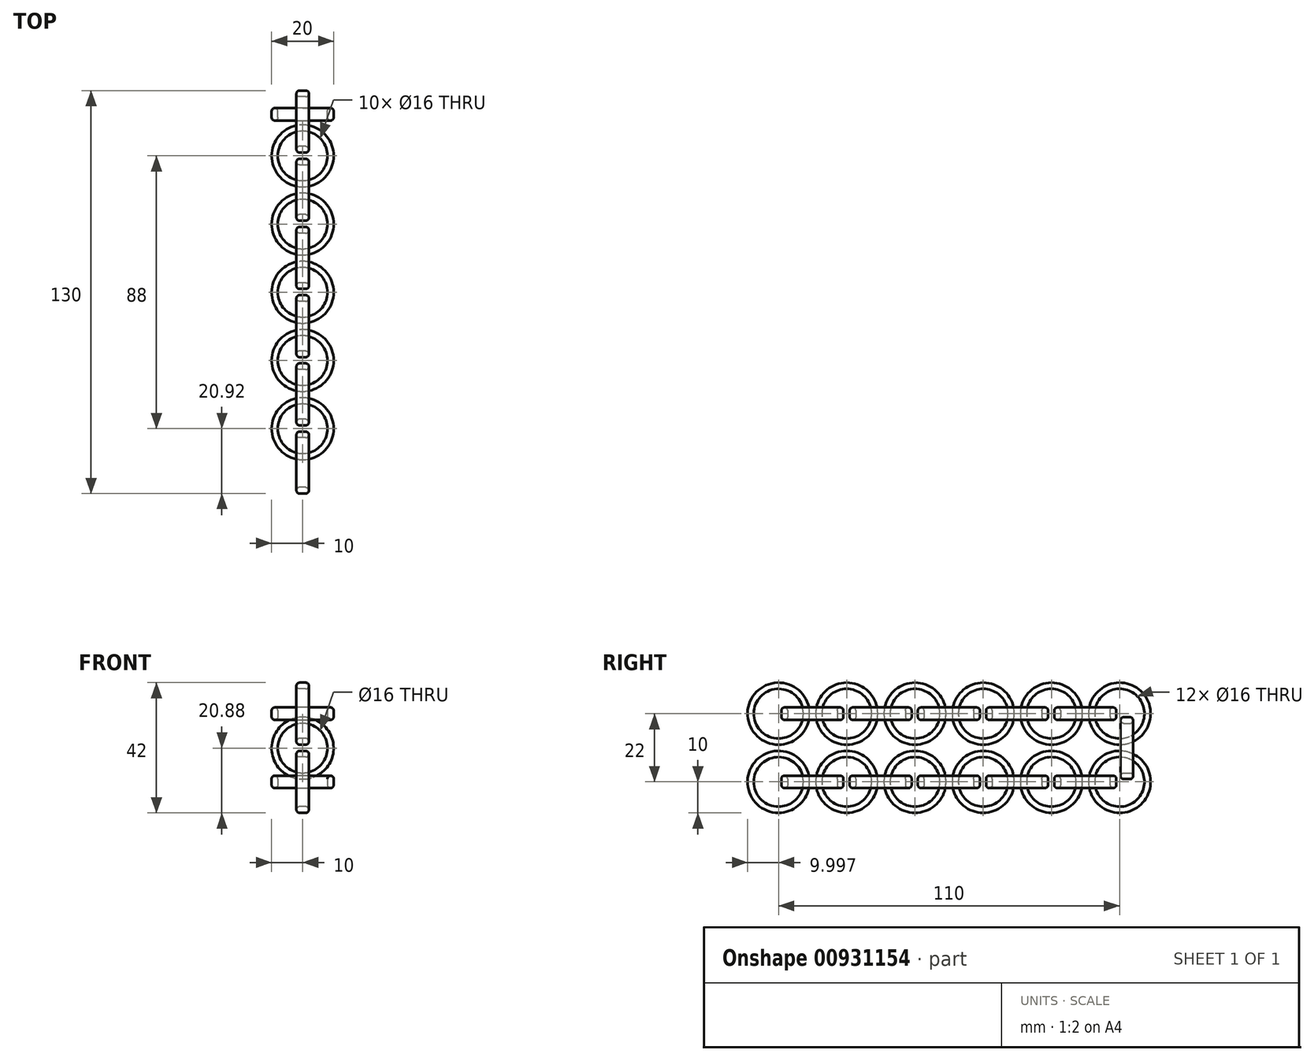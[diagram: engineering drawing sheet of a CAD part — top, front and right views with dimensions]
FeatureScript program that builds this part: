
annotation { "Feature Type Name" : "Feature", "Feature Type Description" : "" }
export const myFeature = defineFeature(function(context is Context, id is Id, definition is map)
    precondition{}
    {
        {
            var Q0;
            Q0=qCreatedBy(makeId("Top.planeOp"),FACE);
            var sketch = newSketch(context, id + "F0", { "sketchPlane" : qUnion([Q0])});
            skCircle(sketch, "E0", {"center": v(0, 0) * mm, "radius": 10 * mm});
            skCircle(sketch, "E1", {"center": v(0, 0) * mm, "radius": 8 * mm});
            skSolve(sketch);
        }
        {
            var Q0;
            Q0=makeQuery(id+"F0.imprint","IMPRINT",FACE,{"disambiguationData":[TD([[makeQuery(id+"F0.imprint","IMPRINT",EDGE,{"derivedFrom":sQuery(id+"F0.wireOp",EDGE,"E0")}),1.0]])]});
            extrude(context, id + "F1", {"entities" : qUnion([Q0]), "endBound" : BoundingType.SYMMETRIC, "depth" : 4 * mm, "offsetDistance" : 25 * mm});
        }
        {
            var Q0;
            Q0=makeQuery(id+"F1.opExtrude","CAP_EDGE",EDGE,{"disambiguationData":[OSD([sQuery(id+"F0.wireOp",EDGE,"E0")])],"isStart":false});
            var Q1;
            Q1=makeQuery(id+"F1.opExtrude","CAP_EDGE",EDGE,{"disambiguationData":[OSD([sQuery(id+"F0.wireOp",EDGE,"E1")])],"isStart":false});
            fillet(context, id + "F2", {"entities" : qUnion([Q0, Q1]), "radius" : 1 * mm, "tangentPropagation" : true, "allowEdgeOverflow" : false});
        }
        {
            var Q0;
            Q0=makeQuery(id+"F1.opExtrude","CAP_EDGE",EDGE,{"disambiguationData":[OSD([sQuery(id+"F0.wireOp",EDGE,"E0")])],"isStart":true});
            var Q1;
            Q1=makeQuery(id+"F1.opExtrude","CAP_EDGE",EDGE,{"disambiguationData":[OSD([sQuery(id+"F0.wireOp",EDGE,"E1")])],"isStart":true});
            fillet(context, id + "F3", {"entities" : qUnion([Q0, Q1]), "radius" : 1 * mm, "tangentPropagation" : true, "allowEdgeOverflow" : false});
        }
        {
            var Q0;
            Q0=makeQuery(id+"F1.opExtrude","SWEPT_BODY",BODY,{"disambiguationData":[OSD([sQuery(id+"F0.wireOp",EDGE,"E0"),sQuery(id+"F0.wireOp",EDGE,"E1")])]});
            transform(context, id + "F4", {"entities" : qUnion([Q0]), "transformType" : TransformType.TRANSLATION_3D, "dx" : 0 * mm, "dy" : 22 * mm, "dz" : 0 * mm, "makeCopy" : true});
        }
        {
            var Q0;
            Q0=makeQuery(id+"F1.opExtrude","SWEPT_BODY",BODY,{"disambiguationData":[OSD([sQuery(id+"F0.wireOp",EDGE,"E0"),sQuery(id+"F0.wireOp",EDGE,"E1")])]});
            transform(context, id + "F5", {"entities" : qUnion([Q0]), "transformType" : TransformType.TRANSLATION_3D, "dx" : 0 * mm, "dy" : 44 * mm, "dz" : 0 * mm, "makeCopy" : true});
        }
        {
            var Q0;
            Q0=makeQuery(id+"F1.opExtrude","SWEPT_BODY",BODY,{"disambiguationData":[OSD([sQuery(id+"F0.wireOp",EDGE,"E0"),sQuery(id+"F0.wireOp",EDGE,"E1")])]});
            transform(context, id + "F6", {"entities" : qUnion([Q0]), "transformType" : TransformType.TRANSLATION_3D, "dx" : 0 * mm, "dy" : -22 * mm, "dz" : 0 * mm, "makeCopy" : true});
        }
        {
            var Q0;
            Q0=makeQuery(id+"F1.opExtrude","SWEPT_BODY",BODY,{"disambiguationData":[OSD([sQuery(id+"F0.wireOp",EDGE,"E0"),sQuery(id+"F0.wireOp",EDGE,"E1")])]});
            transform(context, id + "F7", {"entities" : qUnion([Q0]), "transformType" : TransformType.TRANSLATION_3D, "dx" : 0 * mm, "dy" : -44 * mm, "dz" : 0 * mm, "makeCopy" : true});
        }
        {
            var Q0;
            Q0=makeQuery(id+"F1.opExtrude","SWEPT_BODY",BODY,{"disambiguationData":[OSD([sQuery(id+"F0.wireOp",EDGE,"E0"),sQuery(id+"F0.wireOp",EDGE,"E1")])]});
            transform(context, id + "F8", {"entities" : qUnion([Q0]), "transformType" : TransformType.TRANSLATION_3D, "dx" : 0 * mm, "dy" : -10.6 * mm, "dz" : 0.3 * mm, "makeCopy" : true});
        }
        {
            var Q0;
            Q0=makeQuery(id+"F8.opPattern","COPY",BODY,{"derivedFrom":makeQuery(id+"F1.opExtrude","SWEPT_BODY",BODY,{"disambiguationData":[OSD([sQuery(id+"F0.wireOp",EDGE,"E0"),sQuery(id+"F0.wireOp",EDGE,"E1")])]}),"instanceName":"1"});
            deleteBodies(context, id + "F9", {"entities" : qUnion([Q0])});
        }
        {
            var Q0;
            Q0=qCreatedBy(makeId("Right.planeOp"),FACE);
            var sketch = newSketch(context, id + "F10", { "sketchPlane" : qUnion([Q0])});
            skCircle(sketch, "E2", {"center": v(-10.92, 0) * mm, "radius": 10 * mm});
            skCircle(sketch, "E3", {"center": v(-10.92, 0) * mm, "radius": 8 * mm});
            skSolve(sketch);
        }
        {
            var Q0;
            Q0=makeQuery(id+"F10.imprint","IMPRINT",FACE,{"disambiguationData":[TD([[makeQuery(id+"F10.imprint","IMPRINT",EDGE,{"derivedFrom":sQuery(id+"F10.wireOp",EDGE,"E2")}),1.0]])]});
            extrude(context, id + "F11", {"entities" : qUnion([Q0]), "endBound" : BoundingType.SYMMETRIC, "depth" : 4 * mm, "offsetDistance" : 25 * mm});
        }
        {
            var Q0;
            Q0=makeQuery(id+"F11.opExtrude","CAP_EDGE",EDGE,{"disambiguationData":[OSD([sQuery(id+"F10.wireOp",EDGE,"E2")])],"isStart":false});
            var Q1;
            Q1=makeQuery(id+"F11.opExtrude","CAP_EDGE",EDGE,{"disambiguationData":[OSD([sQuery(id+"F10.wireOp",EDGE,"E3")])],"isStart":false});
            var Q2;
            Q2=makeQuery(id+"F11.opExtrude","CAP_EDGE",EDGE,{"disambiguationData":[OSD([sQuery(id+"F10.wireOp",EDGE,"E3")])],"isStart":true});
            var Q3;
            Q3=makeQuery(id+"F11.opExtrude","CAP_EDGE",EDGE,{"disambiguationData":[OSD([sQuery(id+"F10.wireOp",EDGE,"E2")])],"isStart":true});
            fillet(context, id + "F12", {"entities" : qUnion([Q0, Q1, Q2, Q3]), "radius" : 1 * mm, "tangentPropagation" : true, "allowEdgeOverflow" : false});
        }
        {
            var Q0;
            Q0=makeQuery(id+"F11.opExtrude","SWEPT_BODY",BODY,{"disambiguationData":[OSD([sQuery(id+"F10.wireOp",EDGE,"E2"),sQuery(id+"F10.wireOp",EDGE,"E3")])]});
            transform(context, id + "F13", {"entities" : qUnion([Q0]), "transformType" : TransformType.TRANSLATION_3D, "dx" : 0 * mm, "dy" : 22 * mm, "dz" : 0 * mm, "makeCopy" : true});
        }
        {
            var Q0;
            Q0=makeQuery(id+"F11.opExtrude","SWEPT_BODY",BODY,{"disambiguationData":[OSD([sQuery(id+"F10.wireOp",EDGE,"E2"),sQuery(id+"F10.wireOp",EDGE,"E3")])]});
            transform(context, id + "F14", {"entities" : qUnion([Q0]), "transformType" : TransformType.TRANSLATION_3D, "dx" : 0 * mm, "dy" : 44 * mm, "dz" : 0 * mm, "makeCopy" : true});
        }
        {
            var Q0;
            Q0=makeQuery(id+"F11.opExtrude","SWEPT_BODY",BODY,{"disambiguationData":[OSD([sQuery(id+"F10.wireOp",EDGE,"E2"),sQuery(id+"F10.wireOp",EDGE,"E3")])]});
            transform(context, id + "F15", {"entities" : qUnion([Q0]), "transformType" : TransformType.TRANSLATION_3D, "dx" : 0 * mm, "dy" : -22 * mm, "dz" : 0 * mm, "makeCopy" : true});
        }
        {
            var Q0;
            Q0=makeQuery(id+"F11.opExtrude","SWEPT_BODY",BODY,{"disambiguationData":[OSD([sQuery(id+"F10.wireOp",EDGE,"E2"),sQuery(id+"F10.wireOp",EDGE,"E3")])]});
            transform(context, id + "F16", {"entities" : qUnion([Q0]), "transformType" : TransformType.TRANSLATION_3D, "dx" : 0 * mm, "dy" : -44 * mm, "dz" : 0 * mm, "makeCopy" : true});
        }
        {
            var Q0;
            Q0=makeQuery(id+"F11.opExtrude","SWEPT_BODY",BODY,{"disambiguationData":[OSD([sQuery(id+"F10.wireOp",EDGE,"E2"),sQuery(id+"F10.wireOp",EDGE,"E3")])]});
            transform(context, id + "F17", {"entities" : qUnion([Q0]), "transformType" : TransformType.TRANSLATION_3D, "dx" : 0 * mm, "dy" : 66 * mm, "dz" : 0 * mm, "makeCopy" : true});
        }
        {
            var Q0;
            Q0=makeQuery(id+"F16.opPattern","COPY",BODY,{"derivedFrom":makeQuery(id+"F11.opExtrude","SWEPT_BODY",BODY,{"disambiguationData":[OSD([sQuery(id+"F10.wireOp",EDGE,"E2"),sQuery(id+"F10.wireOp",EDGE,"E3")])]}),"instanceName":"1"});
            transform(context, id + "F18", {"entities" : qUnion([Q0]), "transformType" : TransformType.TRANSLATION_3D, "dx" : 0 * mm, "dy" : 0 * mm, "dz" : 22 * mm, "makeCopy" : true});
        }
        {
            var Q0;
            Q0=makeQuery(id+"F18.opPattern","COPY",BODY,{"derivedFrom":makeQuery(id+"F16.opPattern","COPY",BODY,{"derivedFrom":makeQuery(id+"F11.opExtrude","SWEPT_BODY",BODY,{"disambiguationData":[OSD([sQuery(id+"F10.wireOp",EDGE,"E2"),sQuery(id+"F10.wireOp",EDGE,"E3")])]}),"instanceName":"1"}),"instanceName":"1"});
            transform(context, id + "F19", {"entities" : qUnion([Q0]), "transformType" : TransformType.TRANSLATION_3D, "dx" : 0 * mm, "dy" : 22 * mm, "dz" : 0 * mm, "makeCopy" : true});
        }
        {
            var Q0;
            Q0=makeQuery(id+"F19.opPattern","COPY",BODY,{"derivedFrom":makeQuery(id+"F18.opPattern","COPY",BODY,{"derivedFrom":makeQuery(id+"F16.opPattern","COPY",BODY,{"derivedFrom":makeQuery(id+"F11.opExtrude","SWEPT_BODY",BODY,{"disambiguationData":[OSD([sQuery(id+"F10.wireOp",EDGE,"E2"),sQuery(id+"F10.wireOp",EDGE,"E3")])]}),"instanceName":"1"}),"instanceName":"1"}),"instanceName":"1"});
            transform(context, id + "F20", {"entities" : qUnion([Q0]), "transformType" : TransformType.TRANSLATION_3D, "dx" : 0 * mm, "dy" : 22 * mm, "dz" : 0 * mm, "makeCopy" : true});
        }
        {
            var Q0;
            Q0=makeQuery(id+"F19.opPattern","COPY",BODY,{"derivedFrom":makeQuery(id+"F18.opPattern","COPY",BODY,{"derivedFrom":makeQuery(id+"F16.opPattern","COPY",BODY,{"derivedFrom":makeQuery(id+"F11.opExtrude","SWEPT_BODY",BODY,{"disambiguationData":[OSD([sQuery(id+"F10.wireOp",EDGE,"E2"),sQuery(id+"F10.wireOp",EDGE,"E3")])]}),"instanceName":"1"}),"instanceName":"1"}),"instanceName":"1"});
            transform(context, id + "F21", {"entities" : qUnion([Q0]), "transformType" : TransformType.TRANSLATION_3D, "dx" : 0 * mm, "dy" : 44 * mm, "dz" : 0 * mm, "makeCopy" : true});
        }
        {
            var Q0;
            Q0=makeQuery(id+"F20.opPattern","COPY",BODY,{"derivedFrom":makeQuery(id+"F19.opPattern","COPY",BODY,{"derivedFrom":makeQuery(id+"F18.opPattern","COPY",BODY,{"derivedFrom":makeQuery(id+"F16.opPattern","COPY",BODY,{"derivedFrom":makeQuery(id+"F11.opExtrude","SWEPT_BODY",BODY,{"disambiguationData":[OSD([sQuery(id+"F10.wireOp",EDGE,"E2"),sQuery(id+"F10.wireOp",EDGE,"E3")])]}),"instanceName":"1"}),"instanceName":"1"}),"instanceName":"1"}),"instanceName":"1"});
            transform(context, id + "F22", {"entities" : qUnion([Q0]), "transformType" : TransformType.TRANSLATION_3D, "dx" : 0 * mm, "dy" : 44 * mm, "dz" : 0 * mm, "makeCopy" : true});
        }
        {
            var Q0;
            Q0=makeQuery(id+"F20.opPattern","COPY",BODY,{"derivedFrom":makeQuery(id+"F19.opPattern","COPY",BODY,{"derivedFrom":makeQuery(id+"F18.opPattern","COPY",BODY,{"derivedFrom":makeQuery(id+"F16.opPattern","COPY",BODY,{"derivedFrom":makeQuery(id+"F11.opExtrude","SWEPT_BODY",BODY,{"disambiguationData":[OSD([sQuery(id+"F10.wireOp",EDGE,"E2"),sQuery(id+"F10.wireOp",EDGE,"E3")])]}),"instanceName":"1"}),"instanceName":"1"}),"instanceName":"1"}),"instanceName":"1"});
            transform(context, id + "F23", {"entities" : qUnion([Q0]), "transformType" : TransformType.TRANSLATION_3D, "dx" : 0 * mm, "dy" : 66 * mm, "dz" : 0 * mm, "makeCopy" : true});
        }
        {
            var Q0;
            Q0=makeQuery(id+"F7.opPattern","COPY",BODY,{"derivedFrom":makeQuery(id+"F1.opExtrude","SWEPT_BODY",BODY,{"disambiguationData":[OSD([sQuery(id+"F0.wireOp",EDGE,"E0"),sQuery(id+"F0.wireOp",EDGE,"E1")])]}),"instanceName":"1"});
            transform(context, id + "F24", {"entities" : qUnion([Q0]), "transformType" : TransformType.TRANSLATION_3D, "dx" : 0 * mm, "dy" : 0 * mm, "dz" : 22 * mm, "makeCopy" : true});
        }
        {
            var Q0;
            Q0=makeQuery(id+"F24.opPattern","COPY",BODY,{"derivedFrom":makeQuery(id+"F7.opPattern","COPY",BODY,{"derivedFrom":makeQuery(id+"F1.opExtrude","SWEPT_BODY",BODY,{"disambiguationData":[OSD([sQuery(id+"F0.wireOp",EDGE,"E0"),sQuery(id+"F0.wireOp",EDGE,"E1")])]}),"instanceName":"1"}),"instanceName":"1"});
            transform(context, id + "F25", {"entities" : qUnion([Q0]), "transformType" : TransformType.TRANSLATION_3D, "dx" : 0 * mm, "dy" : 22 * mm, "dz" : 0 * mm, "makeCopy" : true});
        }
        {
            var Q0;
            Q0=makeQuery(id+"F24.opPattern","COPY",BODY,{"derivedFrom":makeQuery(id+"F7.opPattern","COPY",BODY,{"derivedFrom":makeQuery(id+"F1.opExtrude","SWEPT_BODY",BODY,{"disambiguationData":[OSD([sQuery(id+"F0.wireOp",EDGE,"E0"),sQuery(id+"F0.wireOp",EDGE,"E1")])]}),"instanceName":"1"}),"instanceName":"1"});
            transform(context, id + "F26", {"entities" : qUnion([Q0]), "transformType" : TransformType.TRANSLATION_3D, "dx" : 0 * mm, "dy" : 44 * mm, "dz" : 0 * mm, "makeCopy" : true});
        }
        {
            var Q0;
            Q0=makeQuery(id+"F24.opPattern","COPY",BODY,{"derivedFrom":makeQuery(id+"F7.opPattern","COPY",BODY,{"derivedFrom":makeQuery(id+"F1.opExtrude","SWEPT_BODY",BODY,{"disambiguationData":[OSD([sQuery(id+"F0.wireOp",EDGE,"E0"),sQuery(id+"F0.wireOp",EDGE,"E1")])]}),"instanceName":"1"}),"instanceName":"1"});
            transform(context, id + "F27", {"entities" : qUnion([Q0]), "transformType" : TransformType.TRANSLATION_3D, "dx" : 0 * mm, "dy" : 66 * mm, "dz" : 0 * mm, "makeCopy" : true});
        }
        {
            var Q0;
            Q0=makeQuery(id+"F24.opPattern","COPY",BODY,{"derivedFrom":makeQuery(id+"F7.opPattern","COPY",BODY,{"derivedFrom":makeQuery(id+"F1.opExtrude","SWEPT_BODY",BODY,{"disambiguationData":[OSD([sQuery(id+"F0.wireOp",EDGE,"E0"),sQuery(id+"F0.wireOp",EDGE,"E1")])]}),"instanceName":"1"}),"instanceName":"1"});
            transform(context, id + "F28", {"entities" : qUnion([Q0]), "transformType" : TransformType.TRANSLATION_3D, "dx" : 0 * mm, "dy" : 88 * mm, "dz" : 0 * mm, "makeCopy" : true});
        }
        {
            var Q0;
            Q0=qCreatedBy(makeId("Front.planeOp"),FACE);
            var sketch = newSketch(context, id + "F29", { "sketchPlane" : qUnion([Q0])});
            skCircle(sketch, "E4", {"center": v(0, 10.88) * mm, "radius": 10 * mm});
            skCircle(sketch, "E5", {"center": v(0, 10.88) * mm, "radius": 8 * mm});
            skSolve(sketch);
        }
        {
            var Q0;
            Q0 = qSketchRegion(id + "F29", true);
            extrude(context, id + "F30", {"entities" : qUnion([Q0]), "endBound" : BoundingType.SYMMETRIC, "depth" : 4 * mm, "offsetDistance" : 25 * mm});
        }
        {
            var Q0;
            Q0=makeQuery(id+"F30.opExtrude","CAP_EDGE",EDGE,{"disambiguationData":[OSD([sQuery(id+"F29.wireOp",EDGE,"E5")])],"isStart":false});
            var Q1;
            Q1=makeQuery(id+"F30.opExtrude","CAP_EDGE",EDGE,{"disambiguationData":[OSD([sQuery(id+"F29.wireOp",EDGE,"E4")])],"isStart":false});
            var Q2;
            Q2=makeQuery(id+"F30.opExtrude","CAP_EDGE",EDGE,{"disambiguationData":[OSD([sQuery(id+"F29.wireOp",EDGE,"E4")])],"isStart":true});
            var Q3;
            Q3=makeQuery(id+"F30.opExtrude","CAP_EDGE",EDGE,{"disambiguationData":[OSD([sQuery(id+"F29.wireOp",EDGE,"E5")])],"isStart":true});
            fillet(context, id + "F31", {"entities" : qUnion([Q0, Q1, Q2, Q3]), "radius" : 1 * mm, "tangentPropagation" : true, "allowEdgeOverflow" : false});
        }
        {
            var Q0;
            Q0=makeQuery(id+"F30.opExtrude","SWEPT_BODY",BODY,{"disambiguationData":[OSD([sQuery(id+"F29.wireOp",EDGE,"E4"),sQuery(id+"F29.wireOp",EDGE,"E5")])]});
            transform(context, id + "F32", {"entities" : qUnion([Q0]), "transformType" : TransformType.TRANSLATION_3D, "dx" : 0 * mm, "dy" : 57.4 * mm, "dz" : 0 * mm, "makeCopy" : true});
        }
        {
            var Q0;
            Q0=makeQuery(id+"F30.opExtrude","SWEPT_BODY",BODY,{"disambiguationData":[OSD([sQuery(id+"F29.wireOp",EDGE,"E4"),sQuery(id+"F29.wireOp",EDGE,"E5")])]});
            deleteBodies(context, id + "F33", {"entities" : qUnion([Q0])});
        }
    });
